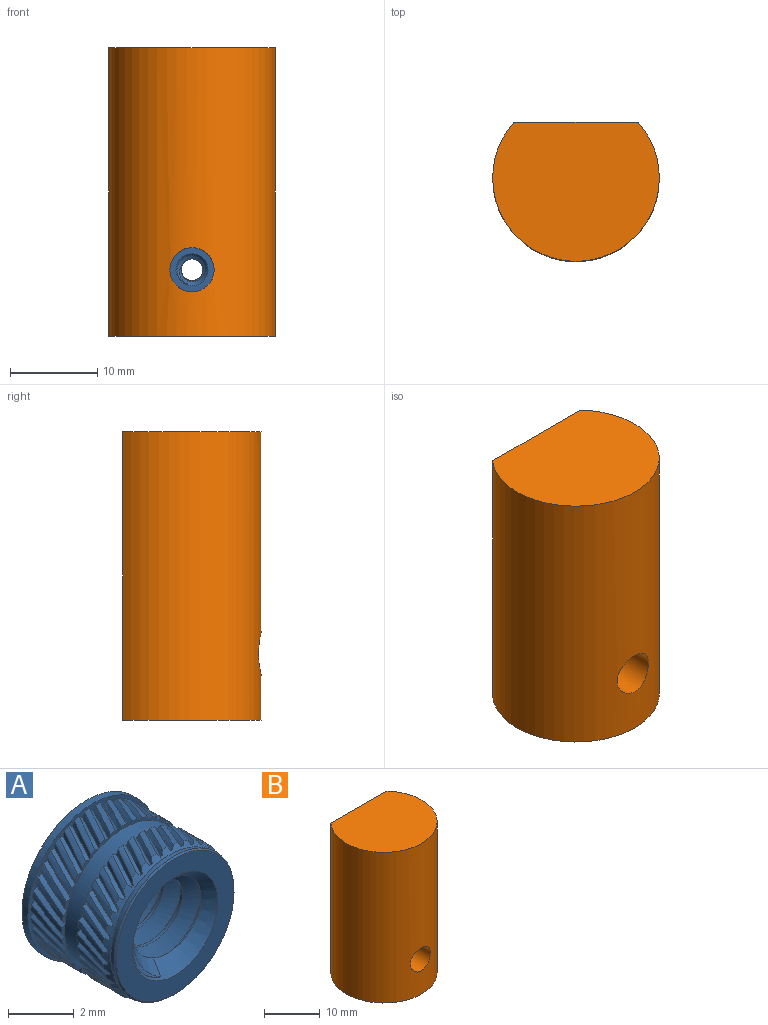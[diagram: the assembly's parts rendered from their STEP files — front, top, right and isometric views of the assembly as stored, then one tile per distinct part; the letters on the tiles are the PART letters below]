
ASSEMBLY  parts=2 mates=1
PART A: 340 faces, bbox 5.6x4.4x5.6 mm
  f0: cylinder r=2.65mm len=1.11mm, axis (0,1,0), area 0.2mm2, adj f105,f106,f152,f302
  f1: cylinder r=2.65mm len=1.11mm, axis (0,1,0), area 0.2mm2, adj f103,f104,f152,f300
  f2: cylinder r=2.65mm len=1.11mm, axis (0,1,0), area 0.2mm2, adj f101,f102,f152,f299
  f3: cylinder r=2.65mm len=1.11mm, axis (0,1,0), area 0.2mm2, adj f99,f100,f152,f297
  f4: cylinder r=2.65mm len=1.11mm, axis (0,1,0), area 0.2mm2, adj f97,f98,f152,f296
  f5: cylinder r=2.65mm len=1.11mm, axis (0,1,0), area 0.2mm2, adj f95,f96,f152,f294
  f6: cylinder r=2.65mm len=1.11mm, axis (0,1,0), area 0.2mm2, adj f93,f94,f152,f293
  f7: cylinder r=2.65mm len=1.11mm, axis (0,1,0), area 0.2mm2, adj f91,f92,f152,f291
  f8: cylinder r=2.65mm len=1.11mm, axis (0,1,0), area 0.2mm2, adj f89,f90,f152,f290
  f9: cylinder r=2.65mm len=1.11mm, axis (0,1,0), area 0.2mm2, adj f87,f88,f152,f288
  f10: cylinder r=2.65mm len=1.11mm, axis (0,1,0), area 0.2mm2, adj f85,f86,f152,f287
  f11: cylinder r=2.65mm len=1.11mm, axis (0,1,0), area 0.2mm2, adj f83,f84,f152,f285
  f12: cylinder r=2.65mm len=1.11mm, axis (0,1,0), area 0.2mm2, adj f81,f82,f152,f284
  f13: cylinder r=2.65mm len=1.11mm, axis (0,1,0), area 0.2mm2, adj f79,f80,f152,f282
  f14: cylinder r=2.65mm len=1.11mm, axis (0,1,0), area 0.2mm2, adj f77,f78,f152,f281
  f15: cylinder r=2.65mm len=1.11mm, axis (0,1,0), area 0.2mm2, adj f75,f76,f152,f279
  f16: cylinder r=2.65mm len=1.11mm, axis (0,1,0), area 0.2mm2, adj f73,f74,f152,f278
  f17: cylinder r=2.65mm len=1.11mm, axis (0,1,0), area 0.2mm2, adj f71,f72,f152,f276
  f18: cylinder r=2.65mm len=1.11mm, axis (0,1,0), area 0.2mm2, adj f69,f70,f152,f275
  f19: cylinder r=2.65mm len=1.11mm, axis (0,1,0), area 0.2mm2, adj f67,f68,f152,f273
  f20: cylinder r=2.65mm len=1.11mm, axis (0,1,0), area 0.2mm2, adj f65,f66,f152,f272
  f21: cylinder r=2.65mm len=1.11mm, axis (0,1,0), area 0.2mm2, adj f63,f64,f152,f270
  f22: cylinder r=2.65mm len=1.11mm, axis (0,1,0), area 0.2mm2, adj f61,f62,f152,f269
  f23: cylinder r=2.65mm len=1.11mm, axis (0,1,0), area 0.2mm2, adj f59,f60,f152,f267
  f24: cylinder r=2.65mm len=1.11mm, axis (0,1,0), area 0.2mm2, adj f57,f58,f152,f268
  f25: cylinder r=2.65mm len=1.11mm, axis (0,1,0), area 0.2mm2, adj f55,f56,f152,f271
  f26: cylinder r=2.65mm len=1.11mm, axis (0,1,0), area 0.2mm2, adj f53,f54,f152,f274
  f27: cylinder r=2.65mm len=1.11mm, axis (0,1,0), area 0.2mm2, adj f51,f52,f152,f277
  f28: cylinder r=2.65mm len=1.11mm, axis (0,1,0), area 0.2mm2, adj f49,f50,f152,f280
  f29: cylinder r=2.65mm len=1.11mm, axis (0,1,0), area 0.2mm2, adj f47,f48,f152,f283
  f30: cylinder r=2.65mm len=1.11mm, axis (0,1,0), area 0.2mm2, adj f45,f46,f152,f286
  f31: cylinder r=2.65mm len=1.11mm, axis (0,1,0), area 0.2mm2, adj f43,f44,f152,f289
  f32: cylinder r=2.65mm len=1.11mm, axis (0,1,0), area 0.2mm2, adj f41,f42,f152,f292
  f33: cylinder r=2.65mm len=1.11mm, axis (0,1,0), area 0.2mm2, adj f39,f40,f152,f295
  f34: cylinder r=2.65mm len=1.11mm, axis (0,1,0), area 0.2mm2, adj f37,f38,f152,f298
  f35: cylinder r=2.65mm len=1.11mm, axis (0,1,0), area 0.2mm2, adj f36,f107,f152,f301
  f36: bspline ~1.37x0.77mm, area 0.2mm2, adj f35,f37,f152,f159,f301
  f37: bspline ~1.37x0.67mm, area 0.2mm2, adj f34,f36,f152,f159,f298
  f38: bspline ~1.37x0.81mm, area 0.2mm2, adj f34,f39,f152,f162,f298
  f39: bspline ~1.37x0.74mm, area 0.2mm2, adj f33,f38,f152,f162,f295
  f40: bspline ~1.37x0.82mm, area 0.2mm2, adj f33,f41,f152,f165,f295
  f41: bspline ~1.37x0.79mm, area 0.2mm2, adj f32,f40,f152,f165,f292
  f42: bspline ~1.37x0.81mm, area 0.2mm2, adj f32,f43,f152,f168,f292
  f43: bspline ~1.37x0.82mm, area 0.2mm2, adj f31,f42,f152,f168,f289
  f44: bspline ~1.37x0.78mm, area 0.2mm2, adj f31,f45,f152,f171,f289
  f45: bspline ~1.37x0.82mm, area 0.2mm2, adj f30,f44,f152,f171,f286
  f46: bspline ~1.37x0.72mm, area 0.2mm2, adj f30,f47,f152,f174,f286
  f47: bspline ~1.37x0.8mm, area 0.2mm2, adj f29,f46,f152,f174,f283
  f48: bspline ~1.37x0.64mm, area 0.2mm2, adj f29,f49,f152,f177,f283
  f49: bspline ~1.37x0.75mm, area 0.2mm2, adj f28,f48,f152,f177,f280
  f50: bspline ~1.37x0.62mm, area 0.2mm2, adj f28,f51,f152,f180,f280
  f51: bspline ~1.37x0.68mm, area 0.2mm2, adj f27,f50,f152,f180,f277
  f52: bspline ~1.37x0.71mm, area 0.2mm2, adj f27,f53,f152,f183,f277
  f53: bspline ~1.37x0.59mm, area 0.2mm2, adj f26,f52,f152,f183,f274
  f54: bspline ~1.37x0.77mm, area 0.2mm2, adj f26,f55,f152,f186,f274
  f55: bspline ~1.37x0.67mm, area 0.2mm2, adj f25,f54,f152,f186,f271
  f56: bspline ~1.37x0.81mm, area 0.2mm2, adj f25,f57,f152,f189,f271
  f57: bspline ~1.37x0.74mm, area 0.2mm2, adj f24,f56,f152,f189,f268
  f58: bspline ~1.37x0.82mm, area 0.2mm2, adj f24,f59,f152,f192,f268
  f59: bspline ~1.37x0.79mm, area 0.2mm2, adj f23,f58,f152,f192,f267
  f60: bspline ~1.37x0.81mm, area 0.2mm2, adj f23,f61,f152,f195,f267
  f61: bspline ~1.37x0.82mm, area 0.2mm2, adj f22,f60,f152,f195,f269
  f62: bspline ~1.37x0.78mm, area 0.2mm2, adj f22,f63,f152,f198,f269
  f63: bspline ~1.37x0.82mm, area 0.2mm2, adj f21,f62,f152,f198,f270
  f64: bspline ~1.37x0.72mm, area 0.2mm2, adj f21,f65,f152,f201,f270
  f65: bspline ~1.37x0.8mm, area 0.2mm2, adj f20,f64,f152,f201,f272
  f66: bspline ~1.37x0.64mm, area 0.2mm2, adj f20,f67,f152,f204,f272
  f67: bspline ~1.37x0.75mm, area 0.2mm2, adj f19,f66,f152,f204,f273
  f68: bspline ~1.37x0.62mm, area 0.2mm2, adj f19,f69,f152,f207,f273
  f69: bspline ~1.37x0.68mm, area 0.2mm2, adj f18,f68,f152,f207,f275
  f70: bspline ~1.37x0.71mm, area 0.2mm2, adj f18,f71,f152,f210,f275
  f71: bspline ~1.37x0.59mm, area 0.2mm2, adj f17,f70,f152,f210,f276
  f72: bspline ~1.37x0.77mm, area 0.2mm2, adj f17,f73,f152,f213,f276
  f73: bspline ~1.37x0.67mm, area 0.2mm2, adj f16,f72,f152,f213,f278
  f74: bspline ~1.37x0.81mm, area 0.2mm2, adj f16,f75,f152,f216,f278
  f75: bspline ~1.37x0.74mm, area 0.2mm2, adj f15,f74,f152,f216,f279
  f76: bspline ~1.37x0.82mm, area 0.2mm2, adj f15,f77,f152,f219,f279
  f77: bspline ~1.37x0.79mm, area 0.2mm2, adj f14,f76,f152,f219,f281
  f78: bspline ~1.37x0.81mm, area 0.2mm2, adj f14,f79,f152,f222,f281
  f79: bspline ~1.37x0.82mm, area 0.2mm2, adj f13,f78,f152,f222,f282
  f80: bspline ~1.37x0.78mm, area 0.2mm2, adj f13,f81,f152,f225,f282
  f81: bspline ~1.37x0.82mm, area 0.2mm2, adj f12,f80,f152,f225,f284
  f82: bspline ~1.37x0.72mm, area 0.2mm2, adj f12,f83,f152,f228,f284
  f83: bspline ~1.37x0.8mm, area 0.2mm2, adj f11,f82,f152,f228,f285
  f84: bspline ~1.37x0.64mm, area 0.2mm2, adj f11,f85,f152,f231,f285
  f85: bspline ~1.37x0.75mm, area 0.2mm2, adj f10,f84,f152,f231,f287
  f86: bspline ~1.37x0.62mm, area 0.2mm2, adj f10,f87,f152,f234,f287
  f87: bspline ~1.37x0.68mm, area 0.2mm2, adj f9,f86,f152,f234,f288
  f88: bspline ~1.37x0.71mm, area 0.2mm2, adj f9,f89,f152,f237,f288
  f89: bspline ~1.37x0.59mm, area 0.2mm2, adj f8,f88,f152,f237,f290
  f90: bspline ~1.37x0.77mm, area 0.2mm2, adj f8,f91,f152,f240,f290
  f91: bspline ~1.37x0.67mm, area 0.2mm2, adj f7,f90,f152,f240,f291
  f92: bspline ~1.37x0.81mm, area 0.2mm2, adj f7,f93,f152,f243,f291
  f93: bspline ~1.37x0.74mm, area 0.2mm2, adj f6,f92,f152,f243,f293
  f94: bspline ~1.37x0.82mm, area 0.2mm2, adj f6,f95,f152,f246,f293
  f95: bspline ~1.37x0.79mm, area 0.2mm2, adj f5,f94,f152,f246,f294
  f96: bspline ~1.37x0.81mm, area 0.2mm2, adj f5,f97,f152,f249,f294
  f97: bspline ~1.37x0.82mm, area 0.2mm2, adj f4,f96,f152,f249,f296
  f98: bspline ~1.37x0.78mm, area 0.2mm2, adj f4,f99,f152,f252,f296
  f99: bspline ~1.37x0.82mm, area 0.2mm2, adj f3,f98,f152,f252,f297
  f100: bspline ~1.37x0.72mm, area 0.2mm2, adj f3,f101,f152,f255,f297
  f101: bspline ~1.37x0.8mm, area 0.2mm2, adj f2,f100,f152,f255,f299
  f102: bspline ~1.37x0.64mm, area 0.2mm2, adj f2,f103,f152,f258,f299
  f103: bspline ~1.37x0.75mm, area 0.2mm2, adj f1,f102,f152,f258,f300
  f104: bspline ~1.37x0.62mm, area 0.2mm2, adj f1,f105,f152,f261,f300
  f105: bspline ~1.37x0.68mm, area 0.2mm2, adj f0,f104,f152,f261,f302
  f106: bspline ~1.37x0.71mm, area 0.2mm2, adj f0,f107,f152,f264,f302
  f107: bspline ~1.37x0.59mm, area 0.2mm2, adj f35,f106,f152,f264,f301
  f108: cylinder r=2.65mm len=1.33mm, axis (0,1,0), area 0.3mm2, adj f150,f263,f265,f339
  f109: cylinder r=2.65mm len=1.33mm, axis (0,1,0), area 0.3mm2, adj f150,f260,f262,f337
  f110: cylinder r=2.65mm len=1.33mm, axis (0,1,0), area 0.3mm2, adj f150,f257,f259,f336
  f111: cylinder r=2.65mm len=1.33mm, axis (0,1,0), area 0.3mm2, adj f150,f254,f256,f334
  f112: cylinder r=2.65mm len=1.33mm, axis (0,1,0), area 0.3mm2, adj f150,f251,f253,f333
  f113: cylinder r=2.65mm len=1.33mm, axis (0,1,0), area 0.3mm2, adj f150,f248,f250,f331
  f114: cylinder r=2.65mm len=1.33mm, axis (0,1,0), area 0.3mm2, adj f150,f245,f247,f330
  f115: cylinder r=2.65mm len=1.33mm, axis (0,1,0), area 0.3mm2, adj f150,f242,f244,f328
  f116: cylinder r=2.65mm len=1.33mm, axis (0,1,0), area 0.3mm2, adj f150,f239,f241,f327
  f117: cylinder r=2.65mm len=1.33mm, axis (0,1,0), area 0.3mm2, adj f150,f236,f238,f325
  f118: cylinder r=2.65mm len=1.33mm, axis (0,1,0), area 0.3mm2, adj f150,f233,f235,f324
  f119: cylinder r=2.65mm len=1.33mm, axis (0,1,0), area 0.3mm2, adj f150,f230,f232,f322
  f120: cylinder r=2.65mm len=1.33mm, axis (0,1,0), area 0.3mm2, adj f150,f227,f229,f321
  f121: cylinder r=2.65mm len=1.33mm, axis (0,1,0), area 0.3mm2, adj f150,f224,f226,f319
  f122: cylinder r=2.65mm len=1.33mm, axis (0,1,0), area 0.3mm2, adj f150,f221,f223,f318
  f123: cylinder r=2.65mm len=1.33mm, axis (0,1,0), area 0.3mm2, adj f150,f218,f220,f316
  f124: cylinder r=2.65mm len=1.33mm, axis (0,1,0), area 0.3mm2, adj f150,f215,f217,f315
  f125: cylinder r=2.65mm len=1.33mm, axis (0,1,0), area 0.3mm2, adj f150,f212,f214,f313
  f126: cylinder r=2.65mm len=1.33mm, axis (0,1,0), area 0.3mm2, adj f150,f209,f211,f312
  f127: cylinder r=2.65mm len=1.33mm, axis (0,1,0), area 0.3mm2, adj f150,f206,f208,f310
  f128: cylinder r=2.65mm len=1.33mm, axis (0,1,0), area 0.3mm2, adj f150,f203,f205,f309
  f129: cylinder r=2.65mm len=1.33mm, axis (0,1,0), area 0.3mm2, adj f150,f200,f202,f307
  f130: cylinder r=2.65mm len=1.33mm, axis (0,1,0), area 0.3mm2, adj f150,f197,f199,f306
  f131: cylinder r=2.65mm len=1.33mm, axis (0,1,0), area 0.3mm2, adj f150,f194,f196,f304
  f132: cylinder r=2.65mm len=1.33mm, axis (0,1,0), area 0.3mm2, adj f150,f191,f193,f305
  f133: cylinder r=2.65mm len=1.33mm, axis (0,1,0), area 0.3mm2, adj f150,f188,f190,f308
  f134: cylinder r=2.65mm len=1.33mm, axis (0,1,0), area 0.3mm2, adj f150,f185,f187,f311
  f135: cylinder r=2.65mm len=1.33mm, axis (0,1,0), area 0.3mm2, adj f150,f182,f184,f314
  f136: cylinder r=2.65mm len=1.33mm, axis (0,1,0), area 0.3mm2, adj f150,f179,f181,f317
  f137: cylinder r=2.65mm len=1.33mm, axis (0,1,0), area 0.3mm2, adj f150,f176,f178,f320
  f138: cylinder r=2.65mm len=1.33mm, axis (0,1,0), area 0.3mm2, adj f150,f173,f175,f323
  f139: cylinder r=2.65mm len=1.33mm, axis (0,1,0), area 0.3mm2, adj f150,f170,f172,f326
  f140: cylinder r=2.65mm len=1.33mm, axis (0,1,0), area 0.3mm2, adj f150,f167,f169,f329
  f141: cylinder r=2.65mm len=1.33mm, axis (0,1,0), area 0.3mm2, adj f150,f164,f166,f332
  f142: cylinder r=2.65mm len=1.33mm, axis (0,1,0), area 0.3mm2, adj f150,f161,f163,f335
  f143: cylinder r=1.24mm len=2.62mm, axis (0,1,0), area 2.5mm2, adj f144,f146,f156,f158
  f144: cone r=1.24mm half-angle=45deg, axis (0,1,0), area 4.8mm2, adj f143,f151,f156,f157,f158
  f145: cone r=1.83mm half-angle=45deg, axis (0,-1,0), area 4mm2, adj f146,f155,f156,f157
  f146: cone r=1.83mm half-angle=45deg, axis (0,-1,0), area 0.8mm2, adj f143,f145,f156,f158
  f147: cylinder r=2.53mm len=5.05mm, axis (0,1,0), area 3.1mm2, adj f152,f154
  f148: cylinder r=2.65mm len=1.33mm, axis (0,1,0), area 0.3mm2, adj f150,f160,f266,f338
  f149: cylinder r=2.78mm len=5.56mm, axis (0,1,0), area 4.4mm2, adj f150,f151
  f150: plane 5.56x5.56mm, normal (0,-1,0), area 2.7mm2, adj f108,f109,f110,f111,f112,f113,f114,f115
  f151: plane 5.56x5.56mm, normal (0,1,0), area 13.8mm2, adj f144,f149
  f152: cone r=2.65mm half-angle=30deg, axis (0,1,0), area 3.2mm2, adj f0,f1,f2,f3,f4,f5,f6,f7
  f153: cone r=2.58mm half-angle=45deg, axis (0,1,0), area 1.2mm2, adj f154,f155
  f154: plane 5.16x5.16mm, normal (0,1,0), area 0.8mm2, adj f147,f153
  f155: plane 5.05x5.05mm, normal (0,-1,0), area 9.5mm2, adj f145,f153
  f156: bspline ~4.09x3.51mm, area 22.4mm2, adj f143,f144,f145,f146,f157
  f157: cylinder r=1.75mm len=3.65mm, axis (0,-1,0), area 5mm2, adj f144,f145,f156,f158
  f158: bspline ~4.09x3.51mm, area 22.3mm2, adj f143,f144,f146,f157
  f159: plane 0.08x0.07mm, normal (0,1,0), area 0mm2, adj f36,f37,f152
  f160: bspline ~1.34x0.81mm, area 0.3mm2, adj f148,f150,f161,f338
  f161: bspline ~1.34x0.78mm, area 0.3mm2, adj f142,f150,f160,f335
  f162: plane 0.09x0.07mm, normal (0,1,0), area 0mm2, adj f38,f39,f152
  f163: bspline ~1.34x0.8mm, area 0.3mm2, adj f142,f150,f164,f335
  f164: bspline ~1.34x0.81mm, area 0.3mm2, adj f141,f150,f163,f332
  f165: plane 0.1x0.06mm, normal (0,1,0), area 0mm2, adj f40,f41,f152
  f166: bspline ~1.34x0.76mm, area 0.3mm2, adj f141,f150,f167,f332
  f167: bspline ~1.34x0.81mm, area 0.3mm2, adj f140,f150,f166,f329
  f168: plane 0.1x0.06mm, normal (0,1,0), area 0mm2, adj f42,f43,f152
  f169: bspline ~1.34x0.7mm, area 0.3mm2, adj f140,f150,f170,f329
  f170: bspline ~1.34x0.78mm, area 0.3mm2, adj f139,f150,f169,f326
  f171: plane 0.1x0.05mm, normal (0,1,0), area 0mm2, adj f44,f45,f152
  f172: bspline ~1.34x0.62mm, area 0.3mm2, adj f139,f150,f173,f326
  f173: bspline ~1.34x0.74mm, area 0.3mm2, adj f138,f150,f172,f323
  f174: plane 0.1x0.06mm, normal (0,1,0), area 0mm2, adj f46,f47,f152
  f175: bspline ~1.34x0.62mm, area 0.3mm2, adj f138,f150,f176,f323
  f176: bspline ~1.34x0.67mm, area 0.3mm2, adj f137,f150,f175,f320
  f177: plane 0.09x0.07mm, normal (0,1,0), area 0mm2, adj f48,f49,f152
  f178: bspline ~1.34x0.7mm, area 0.3mm2, adj f137,f150,f179,f320
  f179: bspline ~1.34x0.58mm, area 0.3mm2, adj f136,f150,f178,f317
  f180: plane 0.08x0.07mm, normal (0,1,0), area 0mm2, adj f50,f51,f152
  f181: bspline ~1.34x0.76mm, area 0.3mm2, adj f136,f150,f182,f317
  f182: bspline ~1.34x0.66mm, area 0.3mm2, adj f135,f150,f181,f314
  f183: plane 0.07x0.07mm, normal (0,1,0), area 0mm2, adj f52,f53,f152
  f184: bspline ~1.34x0.8mm, area 0.3mm2, adj f135,f150,f185,f314
  f185: bspline ~1.34x0.73mm, area 0.3mm2, adj f134,f150,f184,f311
  f186: plane 0.08x0.07mm, normal (0,1,0), area 0mm2, adj f54,f55,f152
  f187: bspline ~1.34x0.81mm, area 0.3mm2, adj f134,f150,f188,f311
  f188: bspline ~1.34x0.78mm, area 0.3mm2, adj f133,f150,f187,f308
  f189: plane 0.09x0.07mm, normal (0,1,0), area 0mm2, adj f56,f57,f152
  f190: bspline ~1.34x0.8mm, area 0.3mm2, adj f133,f150,f191,f308
  f191: bspline ~1.34x0.81mm, area 0.3mm2, adj f132,f150,f190,f305
  f192: plane 0.1x0.06mm, normal (0,1,0), area 0mm2, adj f58,f59,f152
  f193: bspline ~1.34x0.76mm, area 0.3mm2, adj f132,f150,f194,f305
  f194: bspline ~1.34x0.81mm, area 0.3mm2, adj f131,f150,f193,f304
  f195: plane 0.1x0.06mm, normal (0,1,0), area 0mm2, adj f60,f61,f152
  f196: bspline ~1.34x0.7mm, area 0.3mm2, adj f131,f150,f197,f304
  f197: bspline ~1.34x0.78mm, area 0.3mm2, adj f130,f150,f196,f306
  f198: plane 0.1x0.05mm, normal (0,1,0), area 0mm2, adj f62,f63,f152
  f199: bspline ~1.34x0.62mm, area 0.3mm2, adj f130,f150,f200,f306
  f200: bspline ~1.34x0.74mm, area 0.3mm2, adj f129,f150,f199,f307
  f201: plane 0.1x0.06mm, normal (0,1,0), area 0mm2, adj f64,f65,f152
  f202: bspline ~1.34x0.62mm, area 0.3mm2, adj f129,f150,f203,f307
  f203: bspline ~1.34x0.67mm, area 0.3mm2, adj f128,f150,f202,f309
  f204: plane 0.09x0.07mm, normal (0,1,0), area 0mm2, adj f66,f67,f152
  f205: bspline ~1.34x0.7mm, area 0.3mm2, adj f128,f150,f206,f309
  f206: bspline ~1.34x0.58mm, area 0.3mm2, adj f127,f150,f205,f310
  f207: plane 0.08x0.07mm, normal (0,1,0), area 0mm2, adj f68,f69,f152
  f208: bspline ~1.34x0.76mm, area 0.3mm2, adj f127,f150,f209,f310
  f209: bspline ~1.34x0.66mm, area 0.3mm2, adj f126,f150,f208,f312
  f210: plane 0.07x0.07mm, normal (0,1,0), area 0mm2, adj f70,f71,f152
  f211: bspline ~1.34x0.8mm, area 0.3mm2, adj f126,f150,f212,f312
  f212: bspline ~1.34x0.73mm, area 0.3mm2, adj f125,f150,f211,f313
  f213: plane 0.08x0.07mm, normal (0,1,0), area 0mm2, adj f72,f73,f152
  f214: bspline ~1.34x0.81mm, area 0.3mm2, adj f125,f150,f215,f313
  f215: bspline ~1.34x0.78mm, area 0.3mm2, adj f124,f150,f214,f315
  f216: plane 0.09x0.07mm, normal (0,1,0), area 0mm2, adj f74,f75,f152
  f217: bspline ~1.34x0.8mm, area 0.3mm2, adj f124,f150,f218,f315
  f218: bspline ~1.34x0.81mm, area 0.3mm2, adj f123,f150,f217,f316
  f219: plane 0.1x0.06mm, normal (0,1,0), area 0mm2, adj f76,f77,f152
  f220: bspline ~1.34x0.76mm, area 0.3mm2, adj f123,f150,f221,f316
  f221: bspline ~1.34x0.81mm, area 0.3mm2, adj f122,f150,f220,f318
  f222: plane 0.1x0.06mm, normal (0,1,0), area 0mm2, adj f78,f79,f152
  f223: bspline ~1.34x0.7mm, area 0.3mm2, adj f122,f150,f224,f318
  f224: bspline ~1.34x0.78mm, area 0.3mm2, adj f121,f150,f223,f319
  f225: plane 0.1x0.05mm, normal (0,1,0), area 0mm2, adj f80,f81,f152
  f226: bspline ~1.34x0.62mm, area 0.3mm2, adj f121,f150,f227,f319
  f227: bspline ~1.34x0.74mm, area 0.3mm2, adj f120,f150,f226,f321
  f228: plane 0.1x0.06mm, normal (0,1,0), area 0mm2, adj f82,f83,f152
  f229: bspline ~1.34x0.62mm, area 0.3mm2, adj f120,f150,f230,f321
  f230: bspline ~1.34x0.67mm, area 0.3mm2, adj f119,f150,f229,f322
  f231: plane 0.09x0.07mm, normal (0,1,0), area 0mm2, adj f84,f85,f152
  f232: bspline ~1.34x0.7mm, area 0.3mm2, adj f119,f150,f233,f322
  f233: bspline ~1.34x0.58mm, area 0.3mm2, adj f118,f150,f232,f324
  f234: plane 0.08x0.07mm, normal (0,1,0), area 0mm2, adj f86,f87,f152
  f235: bspline ~1.34x0.76mm, area 0.3mm2, adj f118,f150,f236,f324
  f236: bspline ~1.34x0.66mm, area 0.3mm2, adj f117,f150,f235,f325
  f237: plane 0.07x0.07mm, normal (0,1,0), area 0mm2, adj f88,f89,f152
  f238: bspline ~1.34x0.8mm, area 0.3mm2, adj f117,f150,f239,f325
  f239: bspline ~1.34x0.73mm, area 0.3mm2, adj f116,f150,f238,f327
  f240: plane 0.08x0.07mm, normal (0,1,0), area 0mm2, adj f90,f91,f152
  f241: bspline ~1.34x0.81mm, area 0.3mm2, adj f116,f150,f242,f327
  f242: bspline ~1.34x0.78mm, area 0.3mm2, adj f115,f150,f241,f328
  f243: plane 0.09x0.07mm, normal (0,1,0), area 0mm2, adj f92,f93,f152
  f244: bspline ~1.34x0.8mm, area 0.3mm2, adj f115,f150,f245,f328
  f245: bspline ~1.34x0.81mm, area 0.3mm2, adj f114,f150,f244,f330
  f246: plane 0.1x0.06mm, normal (0,1,0), area 0mm2, adj f94,f95,f152
  f247: bspline ~1.34x0.76mm, area 0.3mm2, adj f114,f150,f248,f330
  f248: bspline ~1.34x0.81mm, area 0.3mm2, adj f113,f150,f247,f331
  f249: plane 0.1x0.06mm, normal (0,1,0), area 0mm2, adj f96,f97,f152
  f250: bspline ~1.34x0.7mm, area 0.3mm2, adj f113,f150,f251,f331
  f251: bspline ~1.34x0.78mm, area 0.3mm2, adj f112,f150,f250,f333
  f252: plane 0.1x0.05mm, normal (0,1,0), area 0mm2, adj f98,f99,f152
  f253: bspline ~1.34x0.62mm, area 0.3mm2, adj f112,f150,f254,f333
  f254: bspline ~1.34x0.74mm, area 0.3mm2, adj f111,f150,f253,f334
  f255: plane 0.1x0.06mm, normal (0,1,0), area 0mm2, adj f100,f101,f152
  f256: bspline ~1.34x0.62mm, area 0.3mm2, adj f111,f150,f257,f334
  f257: bspline ~1.34x0.67mm, area 0.3mm2, adj f110,f150,f256,f336
  f258: plane 0.09x0.07mm, normal (0,1,0), area 0mm2, adj f102,f103,f152
  f259: bspline ~1.34x0.7mm, area 0.3mm2, adj f110,f150,f260,f336
  f260: bspline ~1.34x0.58mm, area 0.3mm2, adj f109,f150,f259,f337
  f261: plane 0.08x0.07mm, normal (0,1,0), area 0mm2, adj f104,f105,f152
  f262: bspline ~1.34x0.76mm, area 0.3mm2, adj f109,f150,f263,f337
  f263: bspline ~1.34x0.66mm, area 0.3mm2, adj f108,f150,f262,f339
  f264: plane 0.07x0.07mm, normal (0,1,0), area 0mm2, adj f106,f107,f152
  f265: bspline ~1.34x0.8mm, area 0.3mm2, adj f108,f150,f266,f339
  f266: bspline ~1.34x0.73mm, area 0.3mm2, adj f148,f150,f265,f338
  f267: plane 0.45x0.16mm, normal (0,1,0), area 0mm2, adj f23,f59,f60,f303
  f268: plane 0.44x0.18mm, normal (0,1,0), area 0mm2, adj f24,f57,f58,f303
  f269: plane 0.44x0.21mm, normal (0,1,0), area 0mm2, adj f22,f61,f62,f303
  f270: plane 0.41x0.26mm, normal (0,1,0), area 0mm2, adj f21,f63,f64,f303
  f271: plane 0.43x0.23mm, normal (0,1,0), area 0mm2, adj f25,f55,f56,f303
  f272: plane 0.38x0.3mm, normal (0,1,0), area 0mm2, adj f20,f65,f66,f303
  f273: plane 0.34x0.33mm, normal (0,1,0), area 0mm2, adj f19,f67,f68,f303
  f274: plane 0.4x0.28mm, normal (0,1,0), area 0mm2, adj f26,f53,f54,f303
  f275: plane 0.36x0.31mm, normal (0,1,0), area 0mm2, adj f18,f69,f70,f303
  f276: plane 0.4x0.28mm, normal (0,1,0), area 0mm2, adj f17,f71,f72,f303
  f277: plane 0.36x0.31mm, normal (0,1,0), area 0mm2, adj f27,f51,f52,f303
  f278: plane 0.43x0.23mm, normal (0,1,0), area 0mm2, adj f16,f73,f74,f303
  f279: plane 0.44x0.18mm, normal (0,1,0), area 0mm2, adj f15,f75,f76,f303
  f280: plane 0.34x0.33mm, normal (0,1,0), area 0mm2, adj f28,f49,f50,f303
  f281: plane 0.45x0.16mm, normal (0,1,0), area 0mm2, adj f14,f77,f78,f303
  f282: plane 0.44x0.21mm, normal (0,1,0), area 0mm2, adj f13,f79,f80,f303
  f283: plane 0.38x0.3mm, normal (0,1,0), area 0mm2, adj f29,f47,f48,f303
  f284: plane 0.41x0.26mm, normal (0,1,0), area 0mm2, adj f12,f81,f82,f303
  f285: plane 0.38x0.3mm, normal (0,1,0), area 0mm2, adj f11,f83,f84,f303
  f286: plane 0.41x0.26mm, normal (0,1,0), area 0mm2, adj f30,f45,f46,f303
  f287: plane 0.34x0.33mm, normal (0,1,0), area 0mm2, adj f10,f85,f86,f303
  f288: plane 0.36x0.31mm, normal (0,1,0), area 0mm2, adj f9,f87,f88,f303
  f289: plane 0.44x0.21mm, normal (0,1,0), area 0mm2, adj f31,f43,f44,f303
  f290: plane 0.4x0.28mm, normal (0,1,0), area 0mm2, adj f8,f89,f90,f303
  f291: plane 0.43x0.23mm, normal (0,1,0), area 0mm2, adj f7,f91,f92,f303
  f292: plane 0.45x0.16mm, normal (0,1,0), area 0mm2, adj f32,f41,f42,f303
  f293: plane 0.44x0.18mm, normal (0,1,0), area 0mm2, adj f6,f93,f94,f303
  f294: plane 0.45x0.16mm, normal (0,1,0), area 0mm2, adj f5,f95,f96,f303
  f295: plane 0.44x0.18mm, normal (0,1,0), area 0mm2, adj f33,f39,f40,f303
  f296: plane 0.44x0.21mm, normal (0,1,0), area 0mm2, adj f4,f97,f98,f303
  f297: plane 0.41x0.26mm, normal (0,1,0), area 0mm2, adj f3,f99,f100,f303
  f298: plane 0.43x0.23mm, normal (0,1,0), area 0mm2, adj f34,f37,f38,f303
  f299: plane 0.38x0.3mm, normal (0,1,0), area 0mm2, adj f2,f101,f102,f303
  f300: plane 0.34x0.33mm, normal (0,1,0), area 0mm2, adj f1,f103,f104,f303
  f301: plane 0.4x0.28mm, normal (0,1,0), area 0mm2, adj f35,f36,f107,f303
  f302: plane 0.36x0.31mm, normal (0,1,0), area 0mm2, adj f0,f105,f106,f303
  f303: cylinder r=2.53mm len=5.05mm, axis (0,1,0), area 10.2mm2, adj f267,f268,f269,f270,f271,f272,f273,f274
  f304: plane 0.44x0.2mm, normal (0,-1,0), area 0mm2, adj f131,f194,f196,f303
  f305: plane 0.45x0.14mm, normal (0,-1,0), area 0mm2, adj f132,f191,f193,f303
  f306: plane 0.42x0.25mm, normal (0,-1,0), area 0mm2, adj f130,f197,f199,f303
  f307: plane 0.39x0.29mm, normal (0,-1,0), area 0mm2, adj f129,f200,f202,f303
  f308: plane 0.44x0.2mm, normal (0,-1,0), area 0mm2, adj f133,f188,f190,f303
  f309: plane 0.35x0.32mm, normal (0,-1,0), area 0mm2, adj f128,f203,f205,f303
  f310: plane 0.35x0.32mm, normal (0,-1,0), area 0mm2, adj f127,f206,f208,f303
  f311: plane 0.42x0.25mm, normal (0,-1,0), area 0mm2, adj f134,f185,f187,f303
  f312: plane 0.39x0.29mm, normal (0,-1,0), area 0mm2, adj f126,f209,f211,f303
  f313: plane 0.42x0.25mm, normal (0,-1,0), area 0mm2, adj f125,f212,f214,f303
  f314: plane 0.39x0.29mm, normal (0,-1,0), area 0mm2, adj f135,f182,f184,f303
  f315: plane 0.44x0.2mm, normal (0,-1,0), area 0mm2, adj f124,f215,f217,f303
  f316: plane 0.45x0.14mm, normal (0,-1,0), area 0mm2, adj f123,f218,f220,f303
  f317: plane 0.35x0.32mm, normal (0,-1,0), area 0mm2, adj f136,f179,f181,f303
  f318: plane 0.44x0.2mm, normal (0,-1,0), area 0mm2, adj f122,f221,f223,f303
  f319: plane 0.42x0.25mm, normal (0,-1,0), area 0mm2, adj f121,f224,f226,f303
  f320: plane 0.35x0.32mm, normal (0,-1,0), area 0mm2, adj f137,f176,f178,f303
  f321: plane 0.39x0.29mm, normal (0,-1,0), area 0mm2, adj f120,f227,f229,f303
  f322: plane 0.35x0.32mm, normal (0,-1,0), area 0mm2, adj f119,f230,f232,f303
  f323: plane 0.39x0.29mm, normal (0,-1,0), area 0mm2, adj f138,f173,f175,f303
  f324: plane 0.35x0.32mm, normal (0,-1,0), area 0mm2, adj f118,f233,f235,f303
  f325: plane 0.39x0.29mm, normal (0,-1,0), area 0mm2, adj f117,f236,f238,f303
  f326: plane 0.42x0.25mm, normal (0,-1,0), area 0mm2, adj f139,f170,f172,f303
  f327: plane 0.42x0.25mm, normal (0,-1,0), area 0mm2, adj f116,f239,f241,f303
  f328: plane 0.44x0.2mm, normal (0,-1,0), area 0mm2, adj f115,f242,f244,f303
  f329: plane 0.44x0.2mm, normal (0,-1,0), area 0mm2, adj f140,f167,f169,f303
  f330: plane 0.45x0.14mm, normal (0,-1,0), area 0mm2, adj f114,f245,f247,f303
  f331: plane 0.44x0.2mm, normal (0,-1,0), area 0mm2, adj f113,f248,f250,f303
  f332: plane 0.45x0.14mm, normal (0,-1,0), area 0mm2, adj f141,f164,f166,f303
  f333: plane 0.42x0.25mm, normal (0,-1,0), area 0mm2, adj f112,f251,f253,f303
  f334: plane 0.39x0.29mm, normal (0,-1,0), area 0mm2, adj f111,f254,f256,f303
  f335: plane 0.44x0.2mm, normal (0,-1,0), area 0mm2, adj f142,f161,f163,f303
  f336: plane 0.35x0.32mm, normal (0,-1,0), area 0mm2, adj f110,f257,f259,f303
  f337: plane 0.35x0.32mm, normal (0,-1,0), area 0mm2, adj f109,f260,f262,f303
  f338: plane 0.42x0.25mm, normal (0,-1,0), area 0mm2, adj f148,f160,f266,f303
  f339: plane 0.39x0.29mm, normal (0,-1,0), area 0mm2, adj f108,f263,f265,f303
PART B: 8 faces, bbox 19.1x15.9x33 mm
  f0: cylinder r=2.53mm len=8.67mm, axis (0,1,0), area 118.7mm2, adj f2,f6
  f1: plane 33.02x14.2mm, normal (0,1,0), area 448.8mm2, adj f2,f3,f4,f5
  f2: cylinder r=9.53mm len=33.02mm, axis (0,0,-1), area 1426.9mm2, adj f0,f1,f3,f4
  f3: plane 19.05x15.88mm, normal (0,0,1), area 253.8mm2, adj f1,f2
  f4: plane 19.05x15.88mm, normal (0,0,-1), area 231.5mm2, adj f1,f2,f6
  f5: cylinder r=2.53mm len=5.5mm, axis (0,1,0), area 71mm2, adj f1,f6
  f6: cylinder r=2.67mm len=10.16mm, axis (0,0,-1), area 122.2mm2, adj f0,f4,f5,f7
  f7: plane 5.33x5.33mm, normal (0,0,-1), area 22.3mm2, adj f6
PLACE A t=(-21.52,-4.43,-8.04)mm
PLACE B t=(-21.52,-10.78,-15.66)mm
MATE slider A.f0 <-> B.f0  axis (0,1,0) through (-21.52,-4.43,-8.04)mm
